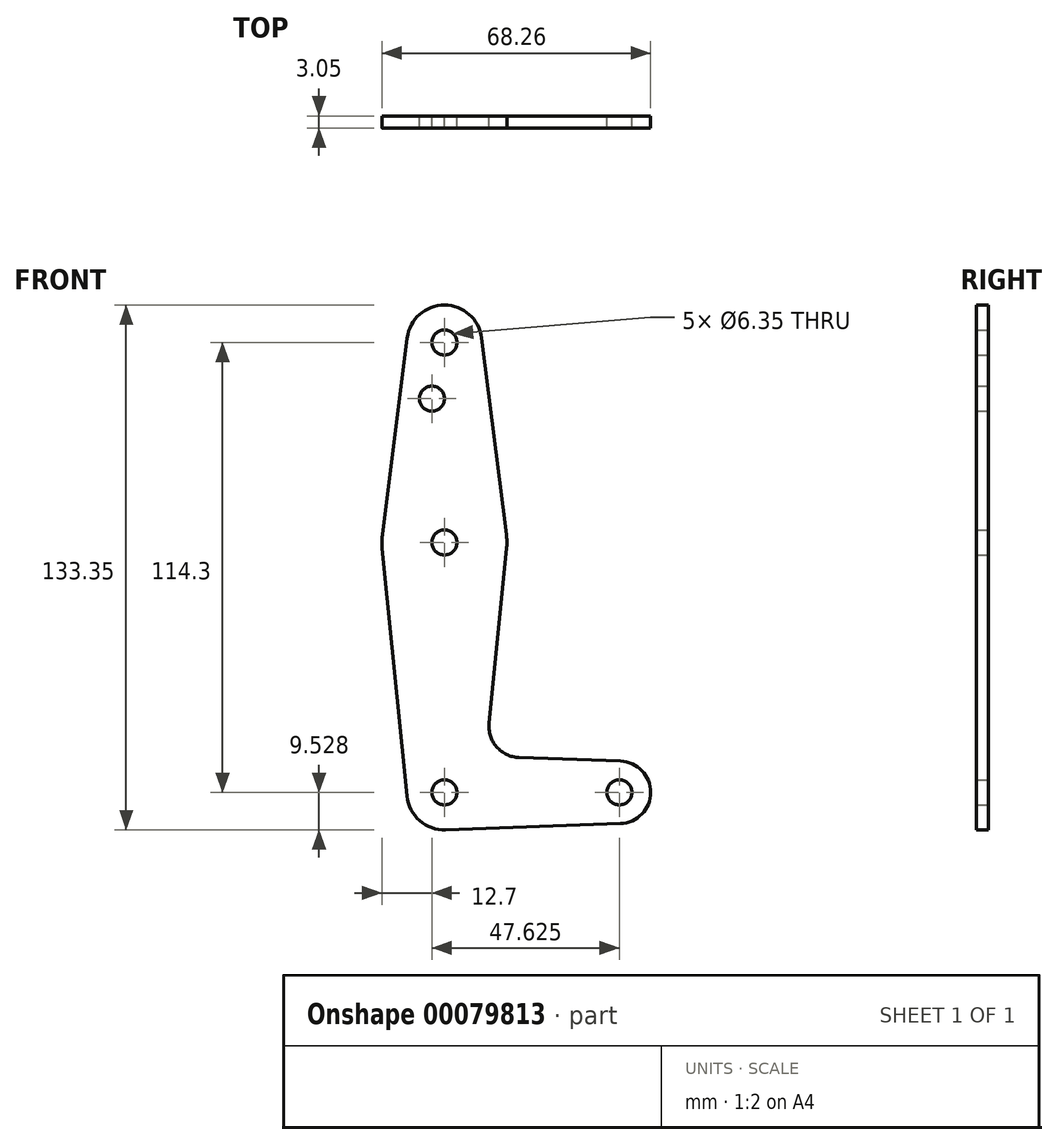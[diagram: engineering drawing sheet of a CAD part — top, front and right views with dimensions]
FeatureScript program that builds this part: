
annotation { "Feature Type Name" : "Feature", "Feature Type Description" : "" }
export const myFeature = defineFeature(function(context is Context, id is Id, definition is map)
    precondition{}
    {
        {
            var Q0;
            Q0=qCreatedBy(makeId("Front.planeOp"),FACE);
            var sketch = newSketch(context, id + "F0", { "sketchPlane" : qUnion([Q0])});
            skCircle(sketch, "E0", {"center": v(-31.63, 72.08) * mm, "radius": 9.53 * mm});
            skLineSegment(sketch, "E1", {"start": v(-31.63, 72.08) * mm, "end": v(-31.63, -42.22) * mm, "construction": true});
            skLineSegment(sketch, "E2", {"start": v(-31.63, -42.22) * mm, "end": v(12.82, -42.22) * mm, "construction": true});
            skCircle(sketch, "E3", {"center": v(-31.63, 21.28) * mm, "radius": 15.88 * mm});
            skCircle(sketch, "E4", {"center": v(-31.63, -42.22) * mm, "radius": 9.53 * mm});
            skCircle(sketch, "E5", {"center": v(12.82, -42.22) * mm, "radius": 7.94 * mm});
            skLineSegment(sketch, "E6", {"start": v(-31.63, 21.28) * mm, "end": v(-31.63, -42.22) * mm, "construction": true});
            skLineSegment(sketch, "E7", {"start": v(-47.42, 19.7) * mm, "end": v(-41.1, -43.17) * mm});
            skLineSegment(sketch, "E8", {"start": v(-41.08, 73.27) * mm, "end": v(-47.38, 23.26) * mm});
            skLineSegment(sketch, "E9", {"start": v(-22.17, 73.27) * mm, "end": v(-15.87, 23.26) * mm});
            skLineSegment(sketch, "E10", {"start": v(-15.83, 19.7) * mm, "end": v(-20.28, -24.63) * mm});
            skLineSegment(sketch, "E11", {"start": v(-31.29, -51.74) * mm, "end": v(13.1, -50.15) * mm});
            skLineSegment(sketch, "E12", {"start": v(-12.66, -33.37) * mm, "end": v(13.1, -34.29) * mm});
            skArc(sketch, "E13.filletArc", {"start": v(-20.28, -24.63) * mm, "mid": v(-18.36, -30.65) * mm, "end": v(-12.66, -33.37) * mm});
            skCircle(sketch, "E14", {"center": v(-34.8, 57.8) * mm, "radius": 3.18 * mm});
            skCircle(sketch, "E15", {"center": v(-31.63, 72.08) * mm, "radius": 3.18 * mm});
            skCircle(sketch, "E16", {"center": v(-31.63, 21.28) * mm, "radius": 3.18 * mm});
            skCircle(sketch, "E17", {"center": v(-31.63, -42.22) * mm, "radius": 3.18 * mm});
            skCircle(sketch, "E18", {"center": v(12.82, -42.22) * mm, "radius": 3.18 * mm});
            skLineSegment(sketch, "E19", {"start": v(-31.63, 21.28) * mm, "end": v(-31.63, 57.8) * mm, "construction": true});
            skSolve(sketch);
        }
        {
            var Q0;
            Q0=makeQuery(id+"F0.imprint","IMPRINT",FACE,{"disambiguationData":[TD([[makeQuery(id+"F0.imprint","IMPRINT",EDGE,{"derivedFrom":sQuery(id+"F0.wireOp",EDGE,"E15")}),-1.0]])]});
            var Q1;
            {var subQ1=sQuery(id+"F0.wireOp",EDGE,"E8");Q1=makeQuery(id+"F0.imprint","IMPRINT",FACE,{"disambiguationData":[TD([[makeQuery(id+"F0.imprint","IMPRINT",EDGE,{"derivedFrom":subQ1}),1.0]])]});}
            var Q2;
            Q2=makeQuery(id+"F0.imprint","IMPRINT",FACE,{"disambiguationData":[TD([[makeQuery(id+"F0.imprint","IMPRINT",EDGE,{"derivedFrom":sQuery(id+"F0.wireOp",EDGE,"E16")}),-1.0]])]});
            var Q3;
            {var subQ0=sQuery(id+"F0.wireOp",EDGE,"E7");Q3=makeQuery(id+"F0.imprint","IMPRINT",FACE,{"disambiguationData":[TD([[makeQuery(id+"F0.imprint","IMPRINT",EDGE,{"derivedFrom":subQ0}),1.0]])]});}
            var Q4;
            Q4=makeQuery(id+"F0.imprint","IMPRINT",FACE,{"disambiguationData":[TD([[makeQuery(id+"F0.imprint","IMPRINT",EDGE,{"derivedFrom":sQuery(id+"F0.wireOp",EDGE,"E17")}),-1.0]])]});
            var Q5;
            Q5=makeQuery(id+"F0.imprint","IMPRINT",FACE,{"disambiguationData":[TD([[makeQuery(id+"F0.imprint","IMPRINT",EDGE,{"derivedFrom":sQuery(id+"F0.wireOp",EDGE,"E18")}),-1.0]])]});
            extrude(context, id + "F1", {"entities" : qUnion([Q0, Q1, Q2, Q3, Q4, Q5]), "depth" : 3.05 * mm});
        }
    });
